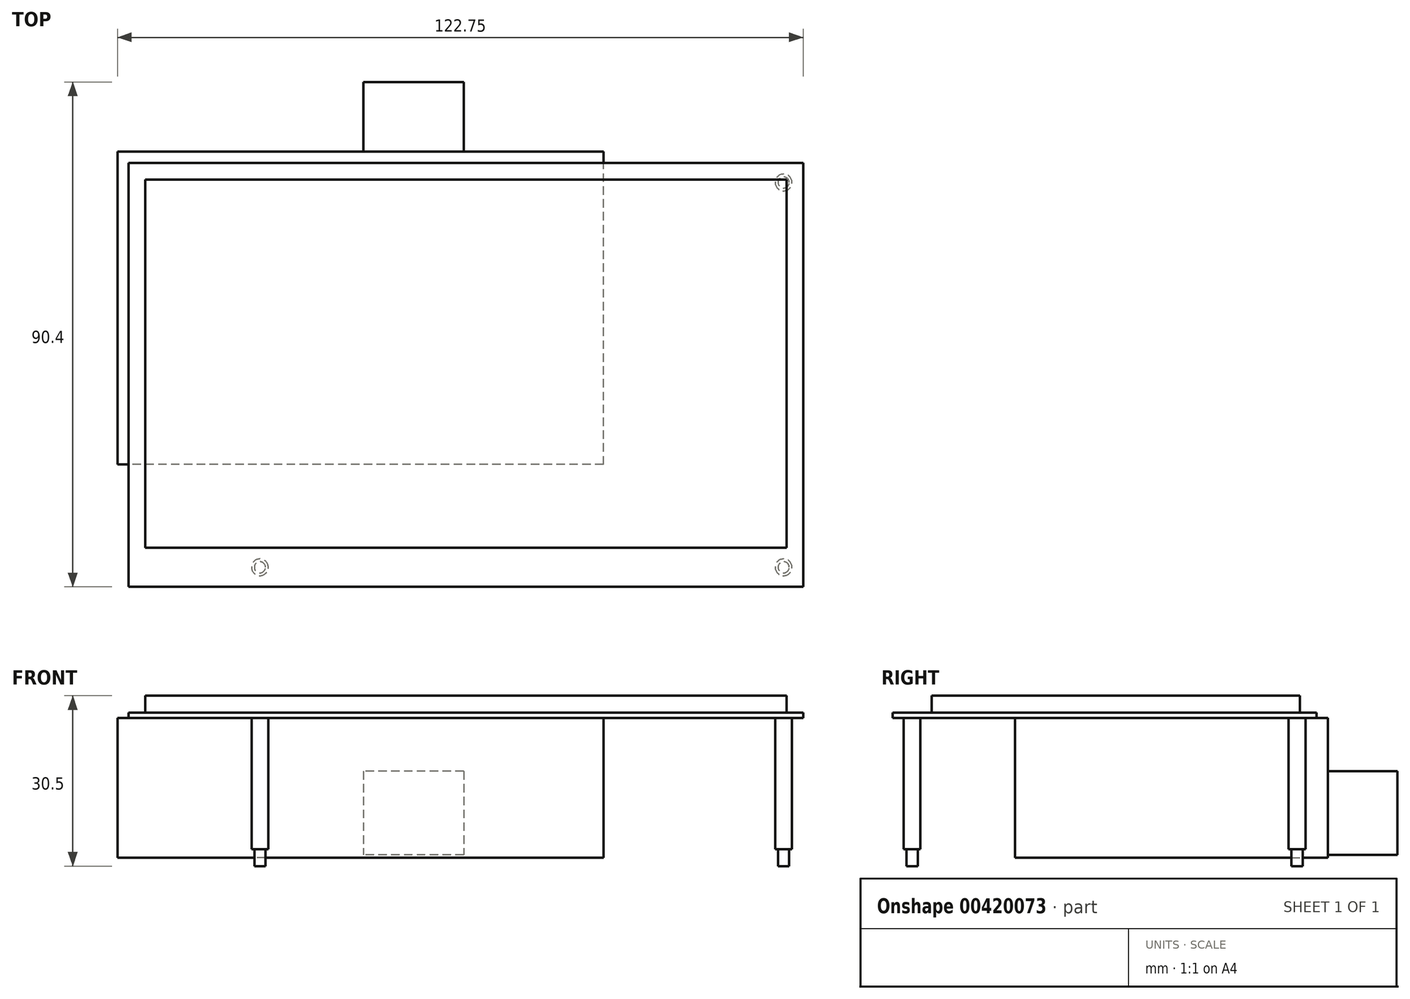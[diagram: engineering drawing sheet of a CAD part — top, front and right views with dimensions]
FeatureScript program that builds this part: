
annotation { "Feature Type Name" : "Feature", "Feature Type Description" : "" }
export const myFeature = defineFeature(function(context is Context, id is Id, definition is map)
    precondition{}
    {
        {
            var Q0;
            Q0=qCreatedBy(makeId("Top.planeOp"),FACE);
            var sketch = newSketch(context, id + "F0", { "sketchPlane" : qUnion([Q0])});
            skLineSegment(sketch, "E0.bottom", {"start": v(0, 0) * mm, "end": v(120.75, 0) * mm});
            skLineSegment(sketch, "E0.top", {"start": v(0, 75.9) * mm, "end": v(120.75, 75.9) * mm});
            skLineSegment(sketch, "E0.left", {"start": v(0, 0) * mm, "end": v(0, 75.9) * mm});
            skLineSegment(sketch, "E0.right", {"start": v(120.75, 0) * mm, "end": v(120.75, 75.9) * mm});
            skSolve(sketch);
        }
        {
            var Q0;
            Q0=makeQuery(id+"F0.imprint","IMPRINT",FACE,{"disambiguationData":[TD([[makeQuery(id+"F0.imprint","IMPRINT",EDGE,{"derivedFrom":sQuery(id+"F0.wireOp",EDGE,"E0.bottom")}),1.0]])]});
            extrude(context, id + "F1", {"entities" : qUnion([Q0]), "depth" : 1 * mm});
        }
        {
            var Q0;
            Q0=makeQuery(id+"F1.opExtrude","CAP_FACE",FACE,{"disambiguationData":[OSD([sQuery(id+"F0.wireOp",EDGE,"E0.bottom"),sQuery(id+"F0.wireOp",EDGE,"E0.top"),sQuery(id+"F0.wireOp",EDGE,"E0.left"),sQuery(id+"F0.wireOp",EDGE,"E0.right")])],"isStart":false});
            var sketch = newSketch(context, id + "F2", { "sketchPlane" : qUnion([Q0])});
            skLineSegment(sketch, "E1.bottom", {"start": v(3, 72.9) * mm, "end": v(117.75, 72.9) * mm});
            skLineSegment(sketch, "E1.top", {"start": v(3, 7) * mm, "end": v(117.75, 7) * mm});
            skLineSegment(sketch, "E1.left", {"start": v(3, 72.9) * mm, "end": v(3, 7) * mm});
            skLineSegment(sketch, "E1.right", {"start": v(117.75, 72.9) * mm, "end": v(117.75, 7) * mm});
            skSolve(sketch);
        }
        {
            var Q0;
            Q0=makeQuery(id+"F2.imprint","IMPRINT",FACE,{"disambiguationData":[TD([[makeQuery(id+"F2.imprint","IMPRINT",EDGE,{"derivedFrom":sQuery(id+"F2.wireOp",EDGE,"E1.bottom")}),-1.0]])]});
            extrude(context, id + "F3", {"entities" : qUnion([Q0]), "operationType" : NewBodyOperationType.ADD, "depth" : 3 * mm});
        }
        {
            var Q0;
            Q0=makeQuery(id+"F1.opExtrude","CAP_FACE",FACE,{"disambiguationData":[OSD([sQuery(id+"F0.wireOp",EDGE,"E0.bottom"),sQuery(id+"F0.wireOp",EDGE,"E0.top"),sQuery(id+"F0.wireOp",EDGE,"E0.left"),sQuery(id+"F0.wireOp",EDGE,"E0.right")])],"isStart":true});
            var sketch = newSketch(context, id + "F4", { "sketchPlane" : qUnion([Q0])});
            skLineSegment(sketch, "E2.bottom", {"start": v(85, -21.9) * mm, "end": v(-2, -21.9) * mm});
            skLineSegment(sketch, "E2.top", {"start": v(85, -77.9) * mm, "end": v(-2, -77.9) * mm});
            skLineSegment(sketch, "E2.left", {"start": v(85, -21.9) * mm, "end": v(85, -77.9) * mm});
            skLineSegment(sketch, "E2.right", {"start": v(-2, -21.9) * mm, "end": v(-2, -77.9) * mm});
            skSolve(sketch);
        }
        {
            var Q0;
            Q0 = qSketchRegion(id + "F4", true);
            extrude(context, id + "F5", {"entities" : qUnion([Q0]), "operationType" : NewBodyOperationType.ADD, "depth" : 25 * mm});
        }
        {
            var Q0;
            Q0=makeQuery(id+"F5.opExtrude","SWEPT_FACE",FACE,{"disambiguationData":[OSD([sQuery(id+"F4.wireOp",EDGE,"E2.top")])]});
            var sketch = newSketch(context, id + "F6", { "sketchPlane" : qUnion([Q0])});
            skLineSegment(sketch, "E3.bottom", {"start": v(-60, -9.5) * mm, "end": v(-42, -9.5) * mm});
            skLineSegment(sketch, "E3.top", {"start": v(-60, -24.5) * mm, "end": v(-42, -24.5) * mm});
            skLineSegment(sketch, "E3.left", {"start": v(-60, -9.5) * mm, "end": v(-60, -24.5) * mm});
            skLineSegment(sketch, "E3.right", {"start": v(-42, -9.5) * mm, "end": v(-42, -24.5) * mm});
            skSolve(sketch);
        }
        {
            var Q0;
            Q0=makeQuery(id+"F6.imprint","IMPRINT",FACE,{"disambiguationData":[TD([[makeQuery(id+"F6.imprint","IMPRINT",EDGE,{"derivedFrom":sQuery(id+"F6.wireOp",EDGE,"E3.bottom")}),-1.0]])]});
            extrude(context, id + "F7", {"entities" : qUnion([Q0]), "operationType" : NewBodyOperationType.ADD, "depth" : 12.5 * mm});
        }
        {
            var Q0;
            Q0=makeQuery(id+"F1.opExtrude","CAP_FACE",FACE,{"disambiguationData":[OSD([sQuery(id+"F0.wireOp",EDGE,"E0.bottom"),sQuery(id+"F0.wireOp",EDGE,"E0.top"),sQuery(id+"F0.wireOp",EDGE,"E0.left"),sQuery(id+"F0.wireOp",EDGE,"E0.right")])],"isStart":true});
            var sketch = newSketch(context, id + "F8", { "sketchPlane" : qUnion([Q0])});
            skCircle(sketch, "E4", {"center": v(23.5, -3.5) * mm, "radius": 1.5 * mm});
            skCircle(sketch, "E5", {"center": v(117.25, -3.5) * mm, "radius": 1.5 * mm});
            skCircle(sketch, "E6", {"center": v(117.25, -72.4) * mm, "radius": 1.5 * mm});
            skSolve(sketch);
        }
        {
            var Q0;
            Q0 = qSketchRegion(id + "F8", true);
            extrude(context, id + "F9", {"entities" : qUnion([Q0]), "operationType" : NewBodyOperationType.ADD, "depth" : 23.5 * mm});
        }
        {
            var Q0;
            Q0=makeQuery(id+"F9.opExtrude","CAP_FACE",FACE,{"disambiguationData":[OSD([sQuery(id+"F8.wireOp",EDGE,"E4")])],"isStart":false});
            var sketch = newSketch(context, id + "F10", { "sketchPlane" : qUnion([Q0])});
            skCircle(sketch, "E7", {"center": v(23.5, -3.5) * mm, "radius": 1 * mm});
            skCircle(sketch, "E8.0", {"center": v(117.25, -3.5) * mm, "radius": 1.5 * mm, "construction": true});
            skCircle(sketch, "E9.0", {"center": v(117.25, -72.4) * mm, "radius": 1.5 * mm, "construction": true});
            skCircle(sketch, "E10", {"center": v(117.25, -3.5) * mm, "radius": 1 * mm});
            skCircle(sketch, "E11", {"center": v(117.25, -72.4) * mm, "radius": 1 * mm});
            skSolve(sketch);
        }
        {
            var Q0;
            Q0 = qSketchRegion(id + "F10", true);
            extrude(context, id + "F11", {"entities" : qUnion([Q0]), "operationType" : NewBodyOperationType.ADD, "depth" : 3 * mm});
        }
    });
